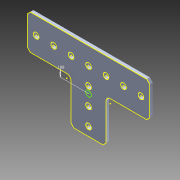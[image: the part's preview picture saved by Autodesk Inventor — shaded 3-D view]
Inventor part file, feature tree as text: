
AUTODESK INVENTOR PART (.ipt)
format: ipt  version: 2014 (Build 180170000, 170)  size: 155,136 bytes
history: native  units: in
note: dims shown in document units (in); Inventor stores cm internally (conversion verified against a paired STEP export)
features: fillet x1, other x1, sketch x1, imported_body x1
ambient origin geometry x8: Origin, YZ Plane, XZ Plane, XY Plane, X Axis, Y Axis, Z Axis, Center Point
bodies: Body1 (feature_tree)
feature tree (4):
  fillet  "Fillet1"  Radius=0.1875in
  other  "217-3557-STEP1"
  sketch  "Sketch1"
  imported_body  "Base1"
